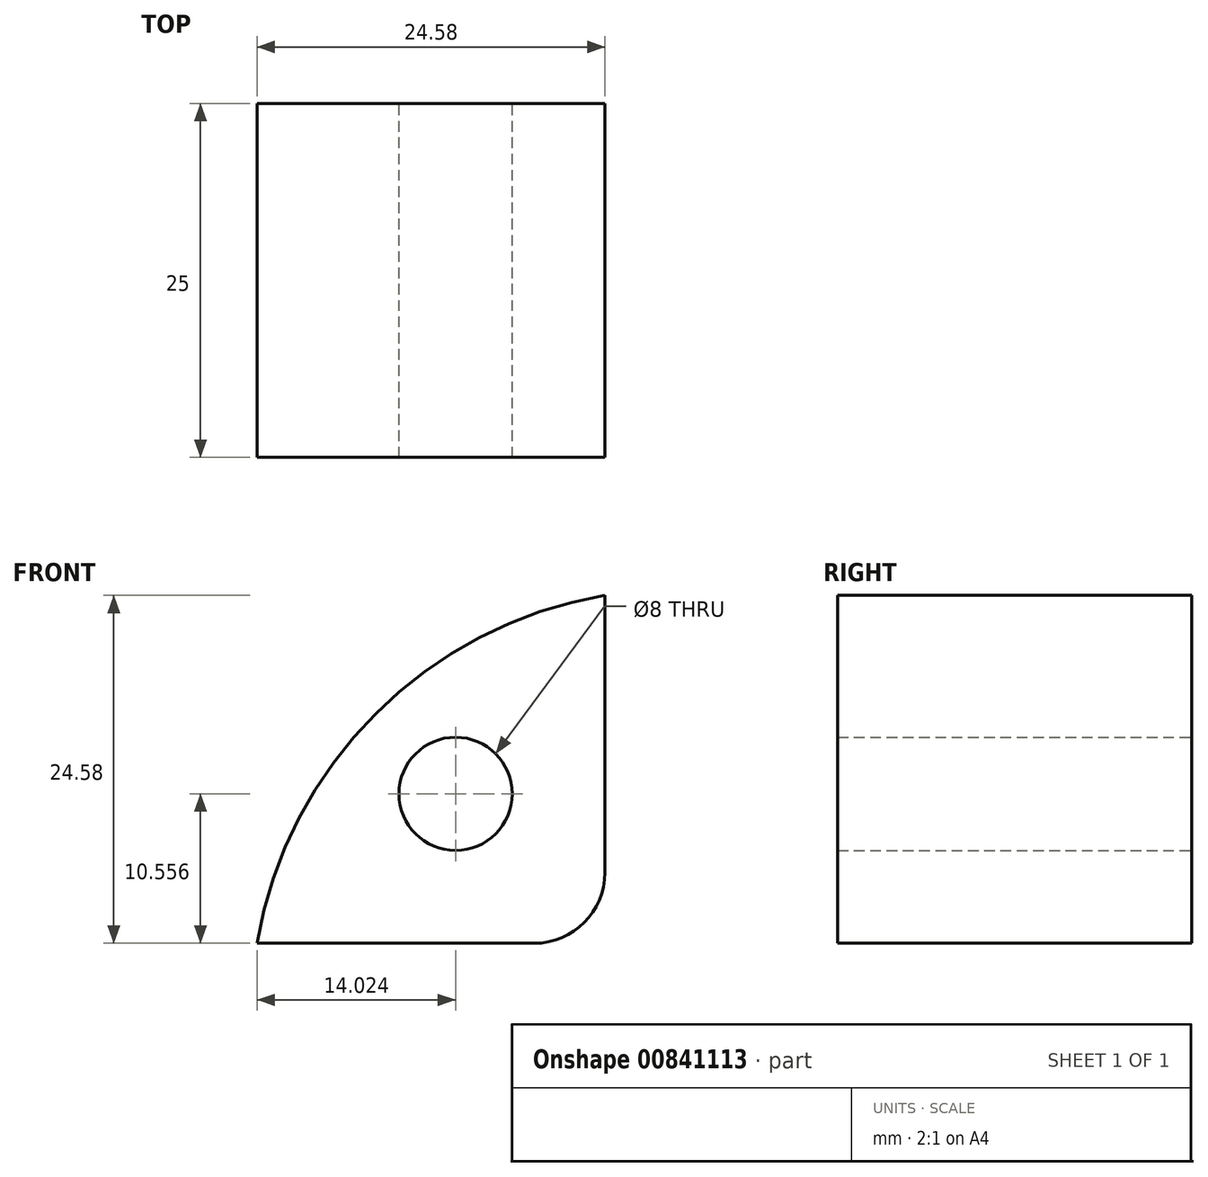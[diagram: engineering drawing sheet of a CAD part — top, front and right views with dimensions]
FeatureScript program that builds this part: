
annotation { "Feature Type Name" : "Feature", "Feature Type Description" : "" }
export const myFeature = defineFeature(function(context is Context, id is Id, definition is map)
    precondition{}
    {
        {
            var Q0;
            Q0=qCreatedBy(makeId("Front.planeOp"),FACE);
            var sketch = newSketch(context, id + "F0", { "sketchPlane" : qUnion([Q0])});
            skCircle(sketch, "E0", {"center": v(0, 0) * mm, "radius": 30 * mm});
            skLineSegment(sketch, "E1.left", {"start": v(5, 29.58) * mm, "end": v(5, -29.58) * mm});
            skLineSegment(sketch, "E1.right", {"start": v(-5, 29.58) * mm, "end": v(-5, -29.58) * mm});
            skLineSegment(sketch, "E2.bottom", {"start": v(29.58, -5) * mm, "end": v(-29.58, -5) * mm});
            skLineSegment(sketch, "E2.top", {"start": v(29.58, 5) * mm, "end": v(-29.58, 5) * mm});
            skPoint(sketch, "E2.right.start.orphan", {"position": v(-31.19, -5) * mm});
            skPoint(sketch, "E3.orphan", {"position": v(-31.19, 5) * mm});
            skPoint(sketch, "E2.left.end.orphan", {"position": v(31.19, 5) * mm});
            skPoint(sketch, "E4.orphan", {"position": v(31.19, -5) * mm});
            skPoint(sketch, "E1.top.end.orphan", {"position": v(-5, -30.7) * mm});
            skPoint(sketch, "E1.top.start.orphan", {"position": v(5, -30.7) * mm});
            skPoint(sketch, "E5.orphan", {"position": v(-5, 30.7) * mm});
            skPoint(sketch, "E6.orphan", {"position": v(5, 30.7) * mm});
            skSolve(sketch);
        }
        {
            var Q0;
            {var subQ0=sQuery(id+"F0.wireOp",EDGE,"E1.right");var subQ1=sQuery(id+"F0.wireOp",EDGE,"E0");var subQ2=makeQuery(id+"F0.imprint","INTERSECT",VERTEX,{"disambiguationData":[OD(0.0)],"derivedFrom":[subQ1,subQ0]});Q0=makeQuery(id+"F0.imprint","IMPRINT",FACE,{"disambiguationData":[TD([[makeQuery(id+"F0.imprint","IMPRINT",EDGE,{"disambiguationData":[TD([[subQ2,-1.0]])],"derivedFrom":subQ1}),1.0]])]});}
            extrude(context, id + "F1", {"entities" : qUnion([Q0]), "depth" : 25 * mm, "offsetDistance" : 25 * mm});
        }
        {
            var Q0;
            Q0=makeQuery(id+"F1.opExtrude","SWEPT_EDGE",EDGE,{"disambiguationData":[OSD([sQuery(id+"F0.wireOp",EDGE,"E1.right"),sQuery(id+"F0.wireOp",EDGE,"E2.top")])]});
            fillet(context, id + "F2", {"entities" : qUnion([Q0]), "radius" : 5 * mm, "tangentPropagation" : true, "allowEdgeOverflow" : false});
        }
        {
            var Q0;
            Q0=qCreatedBy(makeId("Front.planeOp"),FACE);
            var sketch = newSketch(context, id + "F3", { "sketchPlane" : qUnion([Q0])});
            skCircle(sketch, "E7", {"center": v(-15.56, 15.56) * mm, "radius": 4 * mm});
            skLineSegment(sketch, "E8", {"start": v(0, 0) * mm, "end": v(-38.57, 38.57) * mm, "construction": true});
            skSolve(sketch);
        }
        {
            var Q0;
            Q0 = qSketchRegion(id + "F3", true);
            extrude(context, id + "F4", {"entities" : qUnion([Q0]), "operationType" : NewBodyOperationType.REMOVE, "depth" : 47.8 * mm, "offsetDistance" : 25 * mm});
        }
    });
